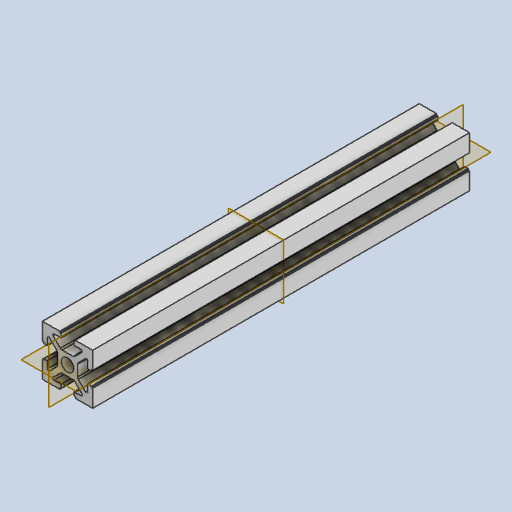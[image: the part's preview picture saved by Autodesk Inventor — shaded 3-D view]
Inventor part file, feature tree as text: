
AUTODESK INVENTOR PART (.ipt)
format: ipt  version: 2025.2 (Build 292293000, 293)  size: 357,888 bytes
history: native  units: mm
features: mirror x2, sketch x2, extrude x1
ambient origin geometry x8: Origin, YZ Plane, XZ Plane, XY Plane, X Axis, Y Axis, Z Axis, Center Point
bodies: Solid1 (feature_tree)
feature tree (5):
  extrude  "Extrusion1"  Depth=10.0mm
  mirror  "Mirror1"
  mirror  "Mirror2"
  sketch  "Sketch2"  dims[d2=5.0mm d3=6.0mm d20=1.0mm d21=2.0mm d25=0.5mm d36=150.0mm d37=0.0mm d38=0.5mm d39=1.0mm]
  sketch  "Sketch1"  dims[d0=20.0mm d1=10.0mm]
